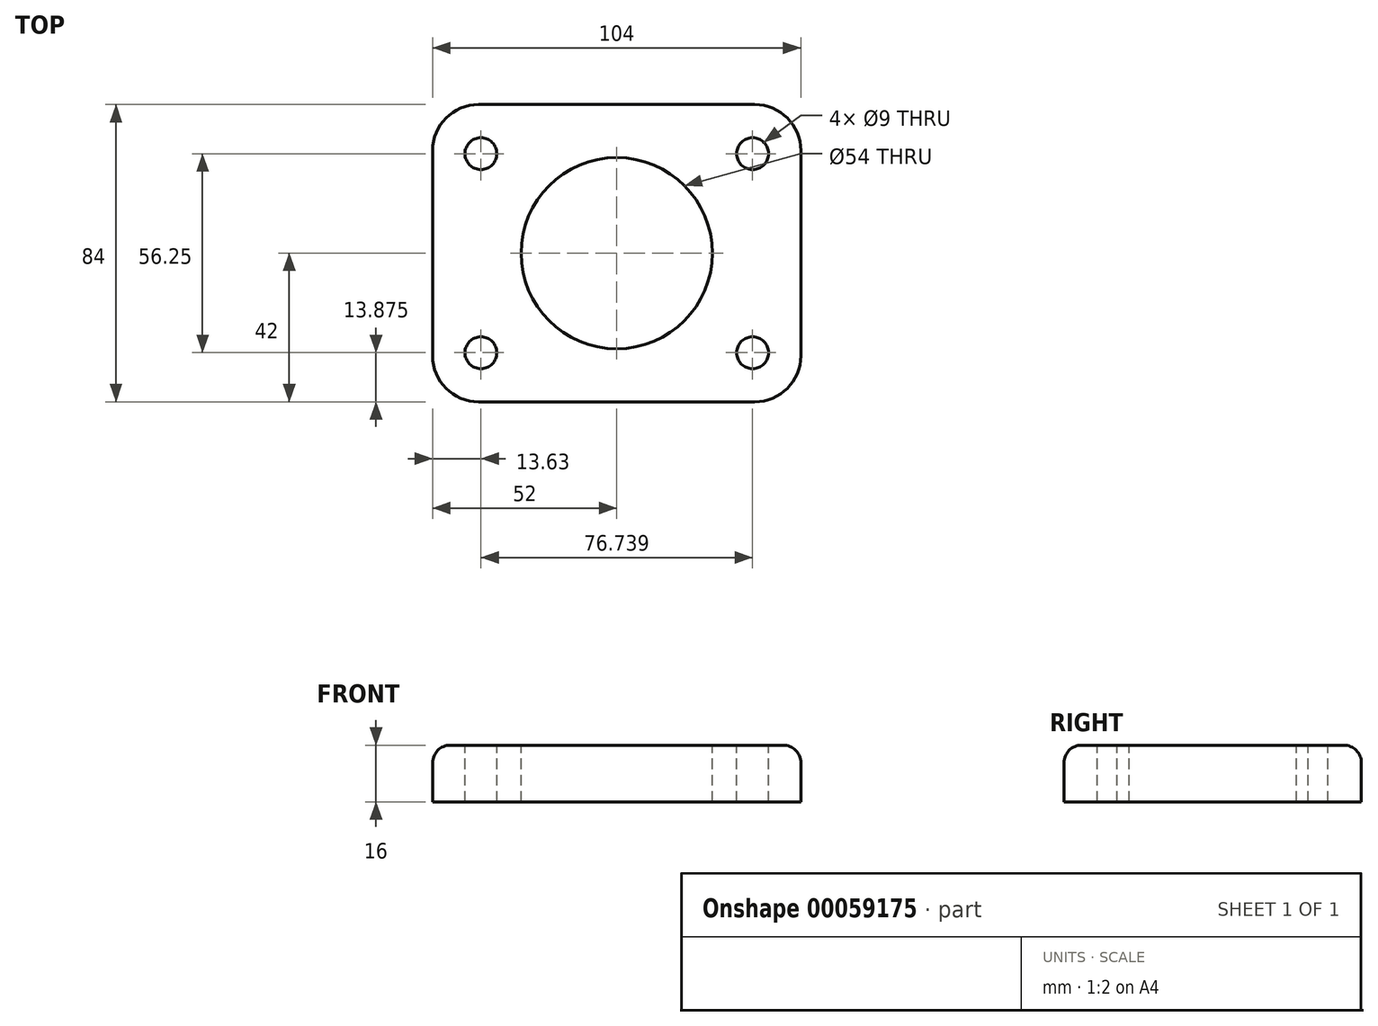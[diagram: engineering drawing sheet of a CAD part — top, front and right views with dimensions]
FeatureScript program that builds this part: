
annotation { "Feature Type Name" : "Feature", "Feature Type Description" : "" }
export const myFeature = defineFeature(function(context is Context, id is Id, definition is map)
    precondition{}
    {
        {
            var Q0;
            Q0=qCreatedBy(makeId("Top.planeOp"),FACE);
            var sketch = newSketch(context, id + "F0", { "sketchPlane" : qUnion([Q0])});
            skLineSegment(sketch, "E0.rect.bottom", {"start": v(52, 42) * mm, "end": v(-52, 42) * mm});
            skLineSegment(sketch, "E0.rect.top", {"start": v(52, -42) * mm, "end": v(-52, -42) * mm});
            skLineSegment(sketch, "E0.rect.left", {"start": v(52, 42) * mm, "end": v(52, -42) * mm});
            skLineSegment(sketch, "E0.rect.right", {"start": v(-52, 42) * mm, "end": v(-52, -42) * mm});
            skPoint(sketch, "E0.rect.middle", {"position": v(0, 0) * mm});
            skPoint(sketch, "E1", {"position": v(32, 27) * mm});
            skSolve(sketch);
        }
        {
            var Q0;
            Q0=makeQuery(id+"F0.imprint","IMPRINT",FACE,{"disambiguationData":[TD([[makeQuery(id+"F0.imprint","IMPRINT",EDGE,{"derivedFrom":sQuery(id+"F0.wireOp",EDGE,"E0.rect.bottom")}),1.0]])]});
            extrude(context, id + "F1", {"entities" : qUnion([Q0]), "oppositeDirection" : true, "depth" : 16 * mm});
        }
        {
            var Q0;
            Q0=makeQuery(id+"F1.opExtrude","CAP_FACE",FACE,{"disambiguationData":[OSD([sQuery(id+"F0.wireOp",EDGE,"E0.rect.bottom"),sQuery(id+"F0.wireOp",EDGE,"E0.rect.top"),sQuery(id+"F0.wireOp",EDGE,"E0.rect.left"),sQuery(id+"F0.wireOp",EDGE,"E0.rect.right")])],"isStart":true});
            var sketch = newSketch(context, id + "F2", { "sketchPlane" : qUnion([Q0])});
            skLineSegment(sketch, "E2", {"start": v(35.49, 25) * mm, "end": v(41.25, 31.25) * mm});
            skArc(sketch, "E3.0.startCap", {"start": v(38.8, 21.95) * mm, "mid": v(32.44, 21.7) * mm, "end": v(32.18, 28.05) * mm});
            skArc(sketch, "E3.0.endCap", {"start": v(37.94, 34.3) * mm, "mid": v(44.3, 34.56) * mm, "end": v(44.56, 28.2) * mm});
            skLineSegment(sketch, "E3.0.left", {"start": v(32.18, 28.05) * mm, "end": v(37.94, 34.3) * mm});
            skLineSegment(sketch, "E3.0.right", {"start": v(38.8, 21.95) * mm, "end": v(44.56, 28.2) * mm});
            skArc(sketch, "E4.MirrorCS", {"start": v(38.8, -21.95) * mm, "mid": v(32.44, -21.7) * mm, "end": v(32.18, -28.05) * mm});
            skLineSegment(sketch, "E5.MirrorCS", {"start": v(35.49, -25) * mm, "end": v(41.25, -31.25) * mm});
            skLineSegment(sketch, "E6.MirrorCS", {"start": v(32.18, -28.05) * mm, "end": v(37.94, -34.3) * mm});
            skLineSegment(sketch, "E7.MirrorCS", {"start": v(38.8, -21.95) * mm, "end": v(44.56, -28.2) * mm});
            skArc(sketch, "E8.MirrorCS", {"start": v(37.94, -34.3) * mm, "mid": v(44.3, -34.56) * mm, "end": v(44.56, -28.2) * mm});
            skLineSegment(sketch, "E9.MirrorCS", {"start": v(-38.8, -21.95) * mm, "end": v(-44.56, -28.2) * mm});
            skArc(sketch, "E10.MirrorCS", {"start": v(-37.94, -34.3) * mm, "mid": v(-44.3, -34.56) * mm, "end": v(-44.56, -28.2) * mm});
            skLineSegment(sketch, "E11.MirrorCS", {"start": v(-32.18, -28.05) * mm, "end": v(-37.94, -34.3) * mm});
            skArc(sketch, "E12.MirrorCS", {"start": v(-37.94, 34.3) * mm, "mid": v(-44.3, 34.56) * mm, "end": v(-44.56, 28.2) * mm});
            skLineSegment(sketch, "E13.MirrorCS", {"start": v(-35.49, -25) * mm, "end": v(-41.25, -31.25) * mm});
            skLineSegment(sketch, "E14.MirrorCS", {"start": v(-35.49, 25) * mm, "end": v(-41.25, 31.25) * mm});
            skArc(sketch, "E15.MirrorCS", {"start": v(-38.8, 21.95) * mm, "mid": v(-32.44, 21.7) * mm, "end": v(-32.18, 28.05) * mm});
            skArc(sketch, "E16.MirrorCS", {"start": v(-38.8, -21.95) * mm, "mid": v(-32.44, -21.7) * mm, "end": v(-32.18, -28.05) * mm});
            skLineSegment(sketch, "E17.MirrorCS", {"start": v(-38.8, 21.95) * mm, "end": v(-44.56, 28.2) * mm});
            skLineSegment(sketch, "E18.MirrorCS", {"start": v(-32.18, 28.05) * mm, "end": v(-37.94, 34.3) * mm});
            skSolve(sketch);
        }
        {
            var Q0;
            Q0=makeQuery(id+"F2.imprint","IMPRINT",FACE,{"disambiguationData":[TD([[makeQuery(id+"F2.imprint","IMPRINT",EDGE,{"derivedFrom":sQuery(id+"F2.wireOp",EDGE,"E3.0.startCap")}),1.0]])]});
            var sketch = newSketch(context, id + "F3", { "sketchPlane" : qUnion([Q0])});
            skCircle(sketch, "E19", {"center": v(38.37, 28.13) * mm, "radius": 4.5 * mm});
            skCircle(sketch, "E20", {"center": v(38.37, -28.13) * mm, "radius": 4.5 * mm});
            skCircle(sketch, "E21", {"center": v(-38.37, 28.13) * mm, "radius": 4.5 * mm});
            skCircle(sketch, "E22", {"center": v(-38.37, -28.13) * mm, "radius": 4.5 * mm});
            skSolve(sketch);
        }
        {
            var Q0;
            Q0=qSketchRegion(id+"F3",true);
            extrude(context, id + "F4", {"entities" : qUnion([Q0]), "operationType" : NewBodyOperationType.REMOVE, "oppositeDirection" : true, "depth" : 25 * mm});
        }
        {
            var Q0;
            Q0=qCreatedBy(makeId("Top.planeOp"),FACE);
            var sketch = newSketch(context, id + "F5", { "sketchPlane" : qUnion([Q0])});
            skCircle(sketch, "E23", {"center": v(0, 0) * mm, "radius": 27 * mm});
            skSolve(sketch);
        }
        {
            var Q0;
            Q0=qSketchRegion(id+"F5",true);
            extrude(context, id + "F6", {"entities" : qUnion([Q0]), "operationType" : NewBodyOperationType.REMOVE, "oppositeDirection" : true, "depth" : 25 * mm});
        }
        {
            var Q0;
            Q0=makeQuery(id+"F1.opExtrude","SWEPT_EDGE",EDGE,{"disambiguationData":[OSD([sQuery(id+"F0.wireOp",EDGE,"E0.rect.bottom"),sQuery(id+"F0.wireOp",EDGE,"E0.rect.right")])]});
            var Q1;
            Q1=makeQuery(id+"F1.opExtrude","SWEPT_EDGE",EDGE,{"disambiguationData":[OSD([sQuery(id+"F0.wireOp",EDGE,"E0.rect.top"),sQuery(id+"F0.wireOp",EDGE,"E0.rect.right")])]});
            var Q2;
            Q2=makeQuery(id+"F1.opExtrude","SWEPT_EDGE",EDGE,{"disambiguationData":[OSD([sQuery(id+"F0.wireOp",EDGE,"E0.rect.top"),sQuery(id+"F0.wireOp",EDGE,"E0.rect.left")])]});
            var Q3;
            Q3=makeQuery(id+"F1.opExtrude","SWEPT_EDGE",EDGE,{"disambiguationData":[OSD([sQuery(id+"F0.wireOp",EDGE,"E0.rect.bottom"),sQuery(id+"F0.wireOp",EDGE,"E0.rect.left")])]});
            fillet(context, id + "F7", {"entities" : qUnion([Q0, Q1, Q2, Q3]), "radius" : 13 * mm, "tangentPropagation" : true, "allowEdgeOverflow" : false});
        }
        {
            var Q0;
            Q0=makeQuery(id+"F1.opExtrude","CAP_EDGE",EDGE,{"disambiguationData":[OSD([sQuery(id+"F0.wireOp",EDGE,"E0.rect.right")])],"isStart":true});
            fillet(context, id + "F8", {"entities" : qUnion([Q0]), "radius" : 5 * mm, "tangentPropagation" : true, "allowEdgeOverflow" : false});
        }
    });
